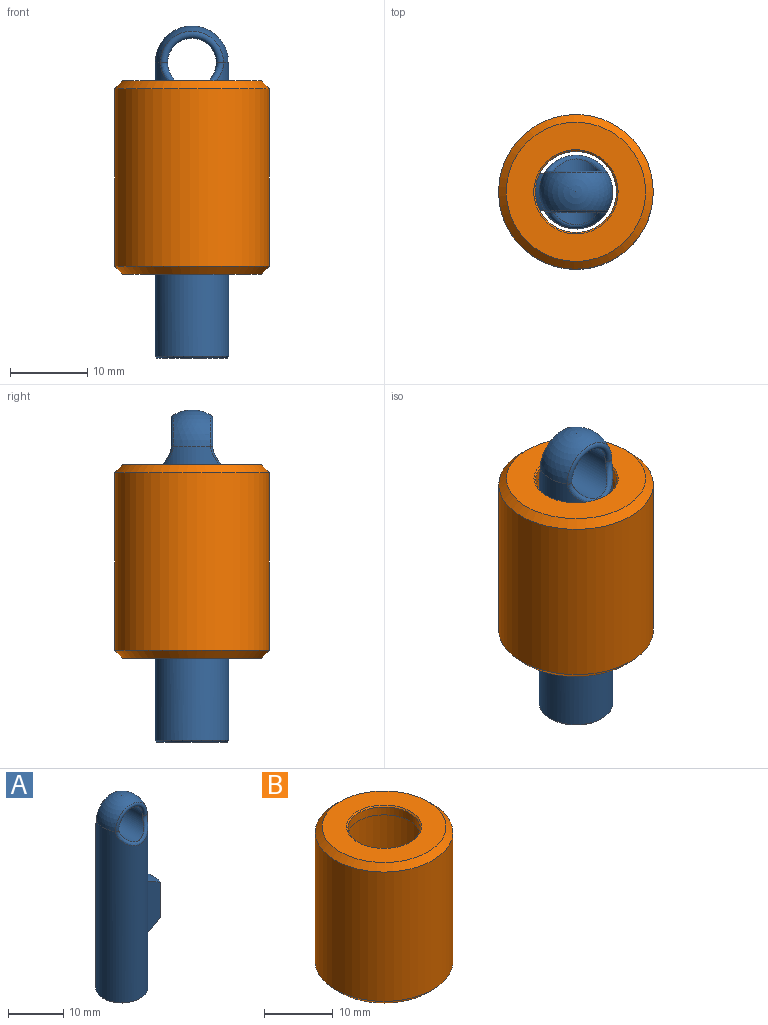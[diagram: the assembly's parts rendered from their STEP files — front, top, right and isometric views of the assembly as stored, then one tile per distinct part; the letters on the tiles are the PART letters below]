
ASSEMBLY  parts=2 mates=1
PART A: 14 faces, bbox 13x9.9x43.3 mm
  f0: cone r=7.9mm half-angle=57.6deg, axis (0,0,1), area 19.6mm2, adj f1,f5,f12,f13
  f1: cylinder r=7.9mm len=7.82mm, axis (0,0,1), area 38.7mm2, adj f0,f2,f12,f13
  f2: cone r=4.75mm half-angle=57.6deg, axis (0,0,-1), area 19.6mm2, adj f1,f5,f12,f13
  f3: sphere r=4.75mm, area 72.6mm2, adj f5,f7,f9
  f4: plane 9.1x9.1mm, normal (0,0,-1), area 65mm2, adj f11
  f5: cylinder r=4.75mm len=37.98mm, axis (0,0,1), area 1020.1mm2, adj f0,f2,f3,f8,f10,f11,f12,f13
  f6: cylinder r=3.15mm len=8.5mm, axis (0,1,0), area 108.4mm2, adj f7,f8,f9,f10
  f7: torus R=3.65mm, axis (0,-1,0), area 14.5mm2, adj f3,f6,f8
  f8: bspline ~8.16x4.14mm, area 11.9mm2, adj f5,f6,f7
  f9: torus R=3.65mm, axis (0,1,0), area 14.5mm2, adj f3,f6,f10
  f10: bspline ~8.16x4.14mm, area 11.9mm2, adj f5,f6,f9
  f11: cone r=4.75mm half-angle=45deg, axis (0,0,1), area 8.3mm2, adj f4,f5
  f12: plane 12.19x3.81mm, normal (0,1,0), area 33.8mm2, adj f0,f1,f2,f5
  f13: plane 12.19x3.81mm, normal (0,-1,0), area 33.8mm2, adj f0,f1,f2,f5
PART B: 12 faces, bbox 20x20x25 mm
  f0: cylinder r=5.25mm len=10.5mm, axis (0,0,1), area 46.2mm2, adj f1,f10
  f1: cone r=5.25mm half-angle=57.6deg, axis (0,0,-1), area 160mm2, adj f0,f2
  f2: cylinder r=8.4mm len=17.8mm, axis (0,0,1), area 939.5mm2, adj f1,f3
  f3: cone r=8.4mm half-angle=57.6deg, axis (0,0,1), area 160mm2, adj f2,f4
  f4: cylinder r=5.25mm len=10.5mm, axis (0,0,1), area 46.2mm2, adj f3,f11
  f5: plane 18x18mm, normal (0,0,-1), area 161.2mm2, adj f8,f11
  f6: cylinder r=10mm len=23mm, axis (0,0,1), area 1445.1mm2, adj f8,f9
  f7: plane 18x18mm, normal (0,0,1), area 161.2mm2, adj f9,f10
  f8: cone r=10mm half-angle=45deg, axis (0,0,1), area 84.4mm2, adj f5,f6
  f9: cone r=9mm half-angle=45deg, axis (0,0,-1), area 84.4mm2, adj f6,f7
  f10: cone r=5.25mm half-angle=45deg, axis (0,0,1), area 9.5mm2, adj f0,f7
  f11: cone r=5.45mm half-angle=45deg, axis (0,0,-1), area 9.5mm2, adj f4,f5
PLACE A rot(axis=(0,0,1),180deg) t=(-0.25,-1.77,-10.72)mm
PLACE B t=(-0.25,-1.77,0.12)mm fixed
MATE slider B.f0 <-> A.f0  axis (0,0,-1) through (-0.25,-1.77,0.12)mm
